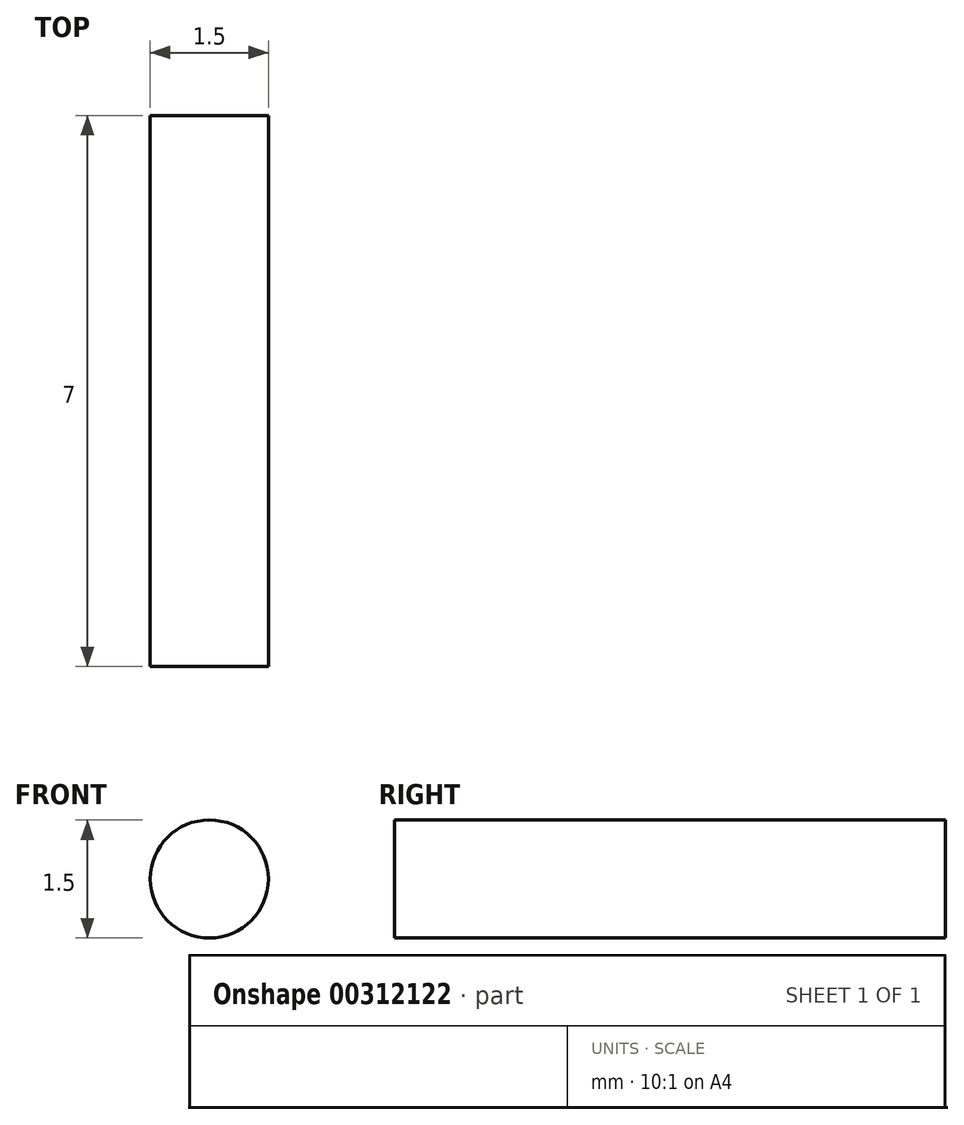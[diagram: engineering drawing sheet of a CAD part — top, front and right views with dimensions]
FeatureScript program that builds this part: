
annotation { "Feature Type Name" : "Feature", "Feature Type Description" : "" }
export const myFeature = defineFeature(function(context is Context, id is Id, definition is map)
    precondition{}
    {
        {
            var Q0;
            Q0=qCreatedBy(makeId("Front.planeOp"),FACE);
            var sketch = newSketch(context, id + "F0", { "sketchPlane" : qUnion([Q0])});
            skArc(sketch, "E0", {"start": v(0, 5) * mm, "mid": v(-5, 0) * mm, "end": v(0, -5) * mm});
            skLineSegment(sketch, "E1", {"start": v(0, 5) * mm, "end": v(30, 5) * mm});
            skLineSegment(sketch, "E2.MirrorCS", {"start": v(0, -5) * mm, "end": v(30, -5) * mm});
            skArc(sketch, "E3", {"start": v(30, -5) * mm, "mid": v(35, 0) * mm, "end": v(30, 5) * mm});
            skSolve(sketch);
        }
        {
            var Q0;
            Q0 = qSketchRegion(id + "F0", true);
            extrude(context, id + "F1", {"entities" : qUnion([Q0]), "depth" : 7 * mm});
        }
        {
            var Q0;
            Q0=makeQuery(id+"F1.opExtrude","SWEPT_FACE",FACE,{"disambiguationData":[OSD([sQuery(id+"F0.wireOp",EDGE,"E1")])]});
            var sketch = newSketch(context, id + "F2", { "sketchPlane" : qUnion([Q0])});
            skLineSegment(sketch, "E4.bottom", {"start": v(35.2, -6) * mm, "end": v(30, -6) * mm});
            skLineSegment(sketch, "E4.top", {"start": v(35.2, -1) * mm, "end": v(30, -1) * mm});
            skLineSegment(sketch, "E4.left", {"start": v(35.2, -6) * mm, "end": v(35.2, -1) * mm});
            skPoint(sketch, "E4.middle", {"position": v(30, -3.5) * mm});
            skLineSegment(sketch, "E5", {"start": v(30, -1) * mm, "end": v(30, -6) * mm});
            skPoint(sketch, "E4.right.end.orphan", {"position": v(24.8, -1) * mm});
            skPoint(sketch, "E6.orphan", {"position": v(24.8, -6) * mm});
            skSolve(sketch);
        }
        {
            var Q0;
            Q0 = qSketchRegion(id + "F2", true);
            extrude(context, id + "F3", {"entities" : qUnion([Q0]), "operationType" : NewBodyOperationType.REMOVE, "oppositeDirection" : true, "depth" : 25 * mm});
        }
        {
            var Q0;
            Q0=makeQuery(id+"F1.opExtrude","CAP_FACE",FACE,{"disambiguationData":[OSD([sQuery(id+"F0.wireOp",EDGE,"E0"),sQuery(id+"F0.wireOp",EDGE,"E1"),sQuery(id+"F0.wireOp",EDGE,"E2.MirrorCS"),sQuery(id+"F0.wireOp",EDGE,"E3")])],"isStart":false});
            var sketch = newSketch(context, id + "F4", { "sketchPlane" : qUnion([Q0])});
            skLineSegment(sketch, "E7.0.0", {"start": v(0, -5) * mm, "end": v(30, -5) * mm});
            skArc(sketch, "E7.0.1", {"start": v(30, -5) * mm, "mid": v(35, 0) * mm, "end": v(30, 5) * mm});
            skLineSegment(sketch, "E7.0.2", {"start": v(30, 5) * mm, "end": v(0, 5) * mm});
            skArc(sketch, "E7.0.3", {"start": v(0, 5) * mm, "mid": v(-5, 0) * mm, "end": v(0, -5) * mm});
            skCircle(sketch, "E8", {"center": v(32.5, 0) * mm, "radius": 0.75 * mm});
            skLineSegment(sketch, "E9", {"start": v(15, 5) * mm, "end": v(15, -5) * mm, "construction": true});
            skCircle(sketch, "E10.MirrorC", {"center": v(-2.5, 0) * mm, "radius": 0.75 * mm});
            skSolve(sketch);
        }
        {
            var Q0;
            Q0=makeQuery(id+"F4.imprint","IMPRINT",FACE,{"disambiguationData":[TD([[makeQuery(id+"F4.imprint","IMPRINT",EDGE,{"derivedFrom":sQuery(id+"F4.wireOp",EDGE,"E8")}),1.0]])]});
            var Q1;
            Q1=makeQuery(id+"F4.imprint","IMPRINT",FACE,{"disambiguationData":[TD([[makeQuery(id+"F4.imprint","IMPRINT",EDGE,{"derivedFrom":sQuery(id+"F4.wireOp",EDGE,"E10.MirrorC")}),-1.0]])]});
            var Q2;
            Q2=sQuery(id+"F4.wireOp",EDGE,"E8");
            extrude(context, id + "F5", {"entities" : qUnion([Q0, Q1]), "operationType" : NewBodyOperationType.REMOVE, "surfaceEntities" : qUnion([Q2]), "oppositeDirection" : true, "depth" : 25 * mm});
        }
    });
